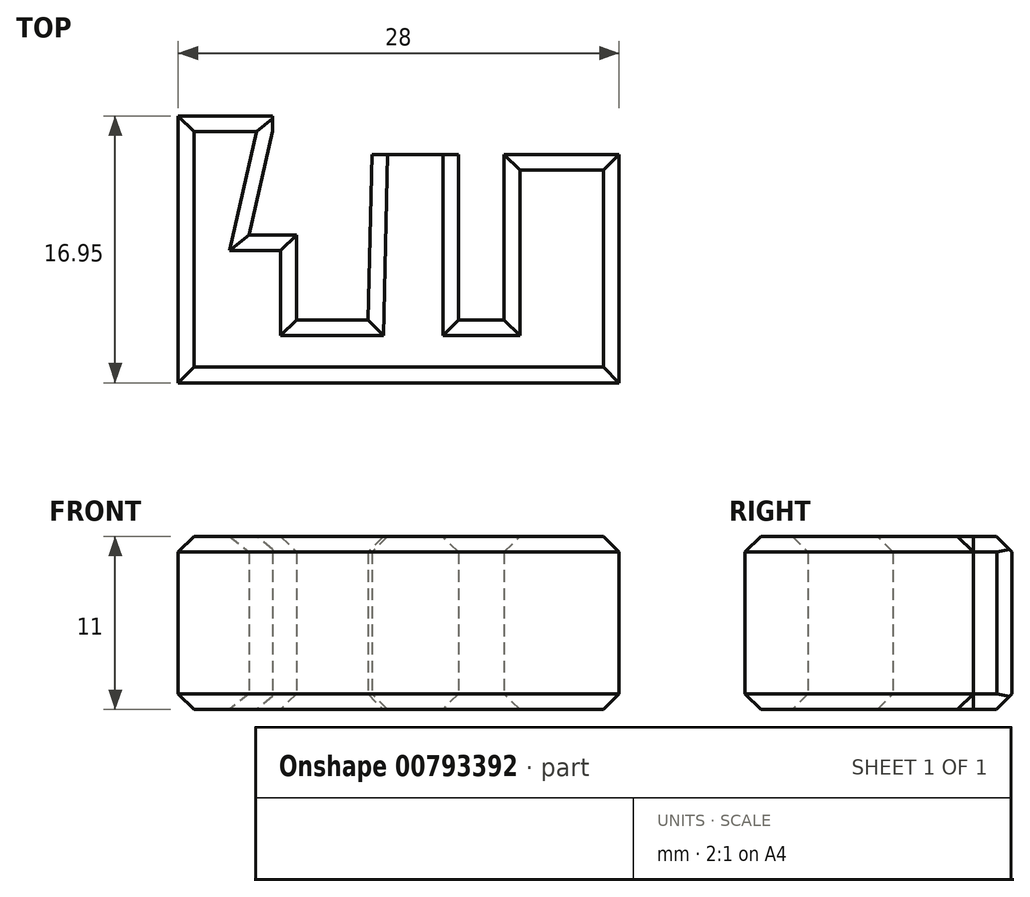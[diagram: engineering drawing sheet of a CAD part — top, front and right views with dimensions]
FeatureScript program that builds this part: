
annotation { "Feature Type Name" : "Feature", "Feature Type Description" : "" }
export const myFeature = defineFeature(function(context is Context, id is Id, definition is map)
    precondition{}
    {
        {
            var Q0;
            Q0=qCreatedBy(makeId("Top.planeOp"),FACE);
            var sketch = newSketch(context, id + "F0", { "sketchPlane" : qUnion([Q0])});
            skLineSegment(sketch, "E0", {"start": v(0, 0) * mm, "end": v(-8.77, 0) * mm});
            skLineSegment(sketch, "E1", {"start": v(-8.77, 0) * mm, "end": v(-6.05, 12) * mm});
            skLineSegment(sketch, "E2", {"start": v(-6.05, 12) * mm, "end": v(-12.05, 12) * mm});
            skLineSegment(sketch, "E3", {"start": v(-12.05, 12) * mm, "end": v(-12.05, -4) * mm});
            skLineSegment(sketch, "E4", {"start": v(-12.05, -4) * mm, "end": v(15.95, -4) * mm});
            skLineSegment(sketch, "E5", {"start": v(15.95, -4) * mm, "end": v(15.95, 10.5) * mm});
            skLineSegment(sketch, "E6", {"start": v(0, 0) * mm, "end": v(0.25, 10.5) * mm});
            skLineSegment(sketch, "E7", {"start": v(0.25, 10.5) * mm, "end": v(5.75, 10.5) * mm});
            skPoint(sketch, "E8", {"position": v(-7.75, 4.5) * mm});
            skLineSegment(sketch, "E9", {"start": v(-7.55, 5.4) * mm, "end": v(-4.55, 5.4) * mm});
            skLineSegment(sketch, "E10", {"start": v(-4.55, 5.4) * mm, "end": v(-4.55, 0) * mm});
            skLineSegment(sketch, "E11", {"start": v(5.75, 10.5) * mm, "end": v(5.75, 0) * mm});
            skLineSegment(sketch, "E12", {"start": v(5.75, 0) * mm, "end": v(8.65, 0) * mm});
            skLineSegment(sketch, "E13", {"start": v(8.65, 0) * mm, "end": v(8.65, 10.5) * mm});
            skLineSegment(sketch, "E14.trimOffspring", {"start": v(8.65, 10.5) * mm, "end": v(15.95, 10.5) * mm});
            skLineSegment(sketch, "E15", {"start": v(5.75, 10.5) * mm, "end": v(0.25, 10.5) * mm});
            skLineSegment(sketch, "E16", {"start": v(-12.05, 12) * mm, "end": v(-12.05, 12.95) * mm});
            skLineSegment(sketch, "E17", {"start": v(-12.05, 12.95) * mm, "end": v(-6.05, 12.95) * mm});
            skLineSegment(sketch, "E18", {"start": v(-6.05, 12.95) * mm, "end": v(-6.05, 12) * mm});
            skSolve(sketch);
        }
        {
            var Q0;
            Q0=makeQuery(id+"F0.imprint","IMPRINT",FACE,{"disambiguationData":[TD([[makeQuery(id+"F0.imprint","IMPRINT",EDGE,{"derivedFrom":sQuery(id+"F0.wireOp",EDGE,"E0")}),1.0]])]});
            var Q1;
            {var subQ4=sQuery(id+"F0.wireOp",EDGE,"E9");Q1=makeQuery(id+"F0.imprint","IMPRINT",FACE,{"disambiguationData":[TD([[makeQuery(id+"F0.imprint","IMPRINT",EDGE,{"derivedFrom":subQ4}),-1.0]])]});}
            var Q2;
            Q2=makeQuery(id+"F0.imprint","IMPRINT",FACE,{"disambiguationData":[TD([[makeQuery(id+"F0.imprint","IMPRINT",EDGE,{"derivedFrom":sQuery(id+"F0.wireOp",EDGE,"E2")}),-1.0]])]});
            extrude(context, id + "F1", {"entities" : qUnion([Q0, Q1, Q2]), "depth" : 11 * mm, "offsetDistance" : 25 * mm});
        }
        {
            var Q0;
            Q0=makeQuery(id+"F1.opExtrude","CAP_EDGE",EDGE,{"disambiguationData":[OSD([sQuery(id+"F0.wireOp",EDGE,"E17")])],"isStart":false});
            var Q1;
            Q1=makeQuery(id+"F1.opExtrude","CAP_EDGE",EDGE,{"disambiguationData":[OSD([sQuery(id+"F0.wireOp",EDGE,"E1")])],"isStart":false});
            var Q2;
            Q2=makeQuery(id+"F1.opExtrude","CAP_EDGE",EDGE,{"disambiguationData":[OSD([sQuery(id+"F0.wireOp",EDGE,"E3"),sQuery(id+"F0.wireOp",EDGE,"E16")])],"isStart":false});
            var Q3;
            Q3=makeQuery(id+"F1.opExtrude","CAP_EDGE",EDGE,{"disambiguationData":[OSD([sQuery(id+"F0.wireOp",EDGE,"E10")])],"isStart":false});
            var Q4;
            Q4=makeQuery(id+"F1.opExtrude","CAP_EDGE",EDGE,{"disambiguationData":[OSD([sQuery(id+"F0.wireOp",EDGE,"E9")])],"isStart":false});
            var Q5;
            Q5=makeQuery(id+"F1.opExtrude","CAP_EDGE",EDGE,{"disambiguationData":[OSD([sQuery(id+"F0.wireOp",EDGE,"E0")])],"isStart":false});
            var Q6;
            Q6=makeQuery(id+"F1.opExtrude","CAP_EDGE",EDGE,{"disambiguationData":[OSD([sQuery(id+"F0.wireOp",EDGE,"E6")])],"isStart":false});
            var Q7;
            Q7=makeQuery(id+"F1.opExtrude","CAP_EDGE",EDGE,{"disambiguationData":[OSD([sQuery(id+"F0.wireOp",EDGE,"E15")])],"isStart":false});
            var Q8;
            Q8=makeQuery(id+"F1.opExtrude","CAP_EDGE",EDGE,{"disambiguationData":[OSD([sQuery(id+"F0.wireOp",EDGE,"E11")])],"isStart":false});
            var Q9;
            Q9=makeQuery(id+"F1.opExtrude","CAP_EDGE",EDGE,{"disambiguationData":[OSD([sQuery(id+"F0.wireOp",EDGE,"E12")])],"isStart":false});
            var Q10;
            Q10=makeQuery(id+"F1.opExtrude","CAP_EDGE",EDGE,{"disambiguationData":[OSD([sQuery(id+"F0.wireOp",EDGE,"E13")])],"isStart":false});
            var Q11;
            Q11=makeQuery(id+"F1.opExtrude","CAP_EDGE",EDGE,{"disambiguationData":[OSD([sQuery(id+"F0.wireOp",EDGE,"E14.trimOffspring")])],"isStart":false});
            var Q12;
            Q12=makeQuery(id+"F1.opExtrude","CAP_EDGE",EDGE,{"disambiguationData":[OSD([sQuery(id+"F0.wireOp",EDGE,"E5")])],"isStart":false});
            var Q13;
            Q13=makeQuery(id+"F1.opExtrude","CAP_EDGE",EDGE,{"disambiguationData":[OSD([sQuery(id+"F0.wireOp",EDGE,"E4")])],"isStart":false});
            chamfer(context, id + "F2", {"entities" : qUnion([Q0, Q1, Q2, Q3, Q4, Q5, Q6, Q7, Q8, Q9, Q10, Q11, Q12, Q13]), "width" : 1 * mm, "tangentPropagation" : true});
        }
        {
            var Q0;
            Q0=makeQuery(id+"F1.opExtrude","CAP_EDGE",EDGE,{"disambiguationData":[OSD([sQuery(id+"F0.wireOp",EDGE,"E14.trimOffspring")])],"isStart":true});
            var Q1;
            Q1=makeQuery(id+"F1.opExtrude","CAP_EDGE",EDGE,{"disambiguationData":[OSD([sQuery(id+"F0.wireOp",EDGE,"E13")])],"isStart":true});
            var Q2;
            Q2=makeQuery(id+"F1.opExtrude","CAP_EDGE",EDGE,{"disambiguationData":[OSD([sQuery(id+"F0.wireOp",EDGE,"E11")])],"isStart":true});
            var Q3;
            Q3=makeQuery(id+"F1.opExtrude","CAP_EDGE",EDGE,{"disambiguationData":[OSD([sQuery(id+"F0.wireOp",EDGE,"E15")])],"isStart":true});
            var Q4;
            Q4=makeQuery(id+"F1.opExtrude","CAP_EDGE",EDGE,{"disambiguationData":[OSD([sQuery(id+"F0.wireOp",EDGE,"E12")])],"isStart":true});
            var Q5;
            Q5=makeQuery(id+"F1.opExtrude","CAP_EDGE",EDGE,{"disambiguationData":[OSD([sQuery(id+"F0.wireOp",EDGE,"E6")])],"isStart":true});
            var Q6;
            Q6=makeQuery(id+"F1.opExtrude","CAP_EDGE",EDGE,{"disambiguationData":[OSD([sQuery(id+"F0.wireOp",EDGE,"E0")])],"isStart":true});
            var Q7;
            Q7=makeQuery(id+"F1.opExtrude","CAP_EDGE",EDGE,{"disambiguationData":[OSD([sQuery(id+"F0.wireOp",EDGE,"E10")])],"isStart":true});
            var Q8;
            Q8=makeQuery(id+"F1.opExtrude","CAP_EDGE",EDGE,{"disambiguationData":[OSD([sQuery(id+"F0.wireOp",EDGE,"E9")])],"isStart":true});
            var Q9;
            Q9=makeQuery(id+"F1.opExtrude","CAP_EDGE",EDGE,{"disambiguationData":[OSD([sQuery(id+"F0.wireOp",EDGE,"E1")])],"isStart":true});
            var Q10;
            Q10=makeQuery(id+"F1.opExtrude","CAP_EDGE",EDGE,{"disambiguationData":[OSD([sQuery(id+"F0.wireOp",EDGE,"E17")])],"isStart":true});
            var Q11;
            Q11=makeQuery(id+"F1.opExtrude","CAP_EDGE",EDGE,{"disambiguationData":[OSD([sQuery(id+"F0.wireOp",EDGE,"E3"),sQuery(id+"F0.wireOp",EDGE,"E16")])],"isStart":true});
            var Q12;
            Q12=makeQuery(id+"F1.opExtrude","CAP_EDGE",EDGE,{"disambiguationData":[OSD([sQuery(id+"F0.wireOp",EDGE,"E4")])],"isStart":true});
            var Q13;
            Q13=makeQuery(id+"F1.opExtrude","CAP_EDGE",EDGE,{"disambiguationData":[OSD([sQuery(id+"F0.wireOp",EDGE,"E5")])],"isStart":true});
            chamfer(context, id + "F3", {"entities" : qUnion([Q0, Q1, Q2, Q3, Q4, Q5, Q6, Q7, Q8, Q9, Q10, Q11, Q12, Q13]), "width" : 1 * mm, "tangentPropagation" : true});
        }
    });
